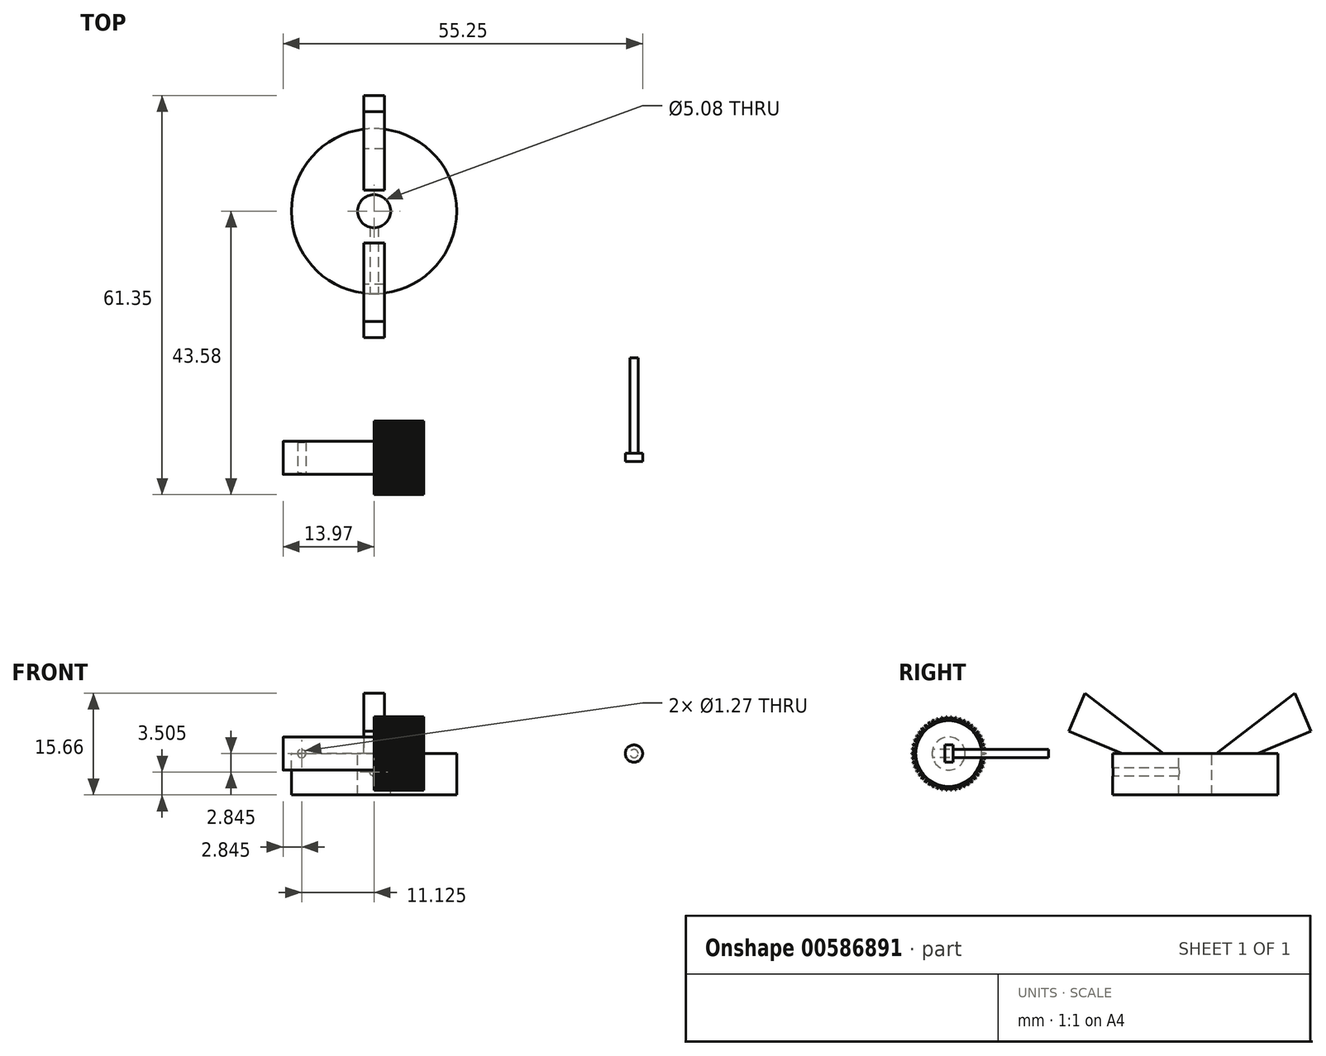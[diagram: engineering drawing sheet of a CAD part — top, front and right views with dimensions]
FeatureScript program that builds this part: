
annotation { "Feature Type Name" : "Feature", "Feature Type Description" : "" }
export const myFeature = defineFeature(function(context is Context, id is Id, definition is map)
    precondition{}
    {
        {
            var Q0;
            Q0=qCreatedBy(makeId("Right.planeOp"),FACE);
            var sketch = newSketch(context, id + "F0", { "sketchPlane" : qUnion([Q0])});
            skCircle(sketch, "E0", {"center": v(0, 0) * mm, "radius": 2.54 * mm});
            skCircle(sketch, "E1", {"center": v(0, 0) * mm, "radius": 5.08 * mm});
            skSolve(sketch);
        }
        {
            var Q0;
            Q0=makeQuery(id+"F0.imprint","IMPRINT",FACE,{"disambiguationData":[TD([[makeQuery(id+"F0.imprint","IMPRINT",EDGE,{"derivedFrom":sQuery(id+"F0.wireOp",EDGE,"E0")}),1.0]])]});
            extrude(context, id + "F1", {"entities" : qUnion([Q0]), "oppositeDirection" : true, "depth" : 13.97 * mm, "offsetDistance" : 25.4 * mm});
        }
        {
            var Q0;
            Q0=makeQuery(id+"F0.imprint","IMPRINT",FACE,{"disambiguationData":[TD([[makeQuery(id+"F0.imprint","IMPRINT",EDGE,{"derivedFrom":sQuery(id+"F0.wireOp",EDGE,"E0")}),-1.0]])]});
            var Q1;
            Q1=makeQuery(id+"F0.imprint","IMPRINT",FACE,{"disambiguationData":[TD([[makeQuery(id+"F0.imprint","IMPRINT",EDGE,{"derivedFrom":sQuery(id+"F0.wireOp",EDGE,"E0")}),1.0]])]});
            extrude(context, id + "F2", {"entities" : qUnion([Q0, Q1]), "operationType" : NewBodyOperationType.ADD, "depth" : 7.62 * mm, "offsetDistance" : 25.4 * mm});
        }
        {
            var Q0;
            Q0=qCreatedBy(makeId("Front.planeOp"),FACE);
            var sketch = newSketch(context, id + "F3", { "sketchPlane" : qUnion([Q0])});
            skPoint(sketch, "E2", {"position": v(-11.13, 0) * mm});
            skSolve(sketch);
        }
        {
            var Q0;
            Q0=qCreatedBy(makeId("Right.planeOp"),FACE);
            var sketch = newSketch(context, id + "F4", { "sketchPlane" : qUnion([Q0])});
            skLineSegment(sketch, "E3.bottom", {"start": v(5.03, -0.13) * mm, "end": v(5.54, -0.13) * mm});
            skLineSegment(sketch, "E3.top", {"start": v(5.03, 0.13) * mm, "end": v(5.54, 0.13) * mm});
            skLineSegment(sketch, "E3.left", {"start": v(5.03, -0.13) * mm, "end": v(5.03, 0.13) * mm});
            skPoint(sketch, "E3.middle", {"position": v(5.28, 0) * mm});
            skLineSegment(sketch, "E4", {"start": v(5.66, 0.06) * mm, "end": v(5.66, -0.06) * mm});
            skLineSegment(sketch, "E5", {"start": v(5.54, 0.13) * mm, "end": v(5.66, 0.06) * mm});
            skLineSegment(sketch, "E6", {"start": v(5.66, -0.06) * mm, "end": v(5.54, -0.13) * mm});
            skSolve(sketch);
        }
        {
            var Q0;
            Q0=makeQuery(id+"F4.imprint","IMPRINT",FACE,{"disambiguationData":[TD([[makeQuery(id+"F4.imprint","IMPRINT",EDGE,{"derivedFrom":sQuery(id+"F4.wireOp",EDGE,"E3.bottom")}),1.0]])]});
            extrude(context, id + "F5", {"entities" : qUnion([Q0]), "operationType" : NewBodyOperationType.ADD, "depth" : 7.62 * mm, "offsetDistance" : 25.4 * mm});
        }
        {
            var Q0;
            Q0=makeQuery(id+"F1.opExtrude","SWEPT_BODY",BODY,{"disambiguationData":[OSD([sQuery(id+"F0.wireOp",EDGE,"E0")])]});
            var Q1;
            Q1=sQuery(id+"F0.wireOp",EDGE,"E0");
            circularPattern(context, id + "F6", {"entities" : qUnion([Q0]), "axis" : qUnion([Q1]), "angle" : 360 * degree, "instanceCount" : 50, "equalSpace" : true});
        }
        {
            var Q0;
            Q0=sQuery(id+"F3.wireOp",VERTEX,"E2");
            var Q1;
            Q1=makeQuery(id+"F6.opPattern","COPY",BODY,{"derivedFrom":makeQuery(id+"F1.opExtrude","SWEPT_BODY",BODY,{"disambiguationData":[OSD([sQuery(id+"F0.wireOp",EDGE,"E0")])]}),"instanceName":"2"});
            hole(context, id + "F7", {"style" : HoleStyle.SIMPLE, "endStyle" : HoleEndStyle.BLIND, "holeDiameter" : 1.27 * mm, "majorDiameter" : 6.35 * mm, "holeDepth" : 508 * mm, "isTappedThrough" : true, "tappedDepth" : 12.7 * mm, "tapClearance" : 3, "startFromSketch" : true, "locations" : qUnion([Q0]), "scope" : qUnion([Q1])});
        }
        {
            var Q0;
            Q0=sQuery(id+"F3.wireOp",VERTEX,"E2");
            var Q1;
            Q1=makeQuery(id+"F6.opPattern","COPY",BODY,{"derivedFrom":makeQuery(id+"F1.opExtrude","SWEPT_BODY",BODY,{"disambiguationData":[OSD([sQuery(id+"F0.wireOp",EDGE,"E0")])]}),"instanceName":"2"});
            hole(context, id + "F8", {"style" : HoleStyle.SIMPLE, "endStyle" : HoleEndStyle.BLIND, "oppositeDirection" : true, "holeDiameter" : 1.27 * mm, "majorDiameter" : 6.35 * mm, "holeDepth" : 508 * mm, "isTappedThrough" : true, "tappedDepth" : 12.7 * mm, "tapClearance" : 3, "startFromSketch" : true, "locations" : qUnion([Q0]), "scope" : qUnion([Q1])});
        }
        {
            var Q0;
            Q0=qCreatedBy(makeId("Right.planeOp"),FACE);
            var sketch = newSketch(context, id + "F9", { "sketchPlane" : qUnion([Q0])});
            skLineSegment(sketch, "E7", {"start": v(20.96, 9.31) * mm, "end": v(18.49, 3.46) * mm});
            skLineSegment(sketch, "E8", {"start": v(47.5, 0) * mm, "end": v(55.7, 3.46) * mm});
            skLineSegment(sketch, "E9", {"start": v(55.7, 3.46) * mm, "end": v(53.22, 9.31) * mm});
            skLineSegment(sketch, "E10", {"start": v(53.22, 9.31) * mm, "end": v(41.16, 0) * mm});
            skLineSegment(sketch, "E11", {"start": v(20.96, 9.31) * mm, "end": v(33.02, 0) * mm});
            skLineSegment(sketch, "E12", {"start": v(33.02, 0) * mm, "end": v(26.67, 0) * mm});
            skLineSegment(sketch, "E13", {"start": v(26.67, 0) * mm, "end": v(18.49, 3.46) * mm});
            skLineSegment(sketch, "E14", {"start": v(41.16, 0) * mm, "end": v(47.5, 0) * mm});
            skLineSegment(sketch, "E15", {"start": v(24.39, 46.4) * mm, "end": v(24.39, 46.4) * mm});
            skSolve(sketch);
        }
        {
            var Q0;
            Q0=qCreatedBy(makeId("Top.planeOp"),FACE);
            var sketch = newSketch(context, id + "F10", { "sketchPlane" : qUnion([Q0])});
            skCircle(sketch, "E16", {"center": v(0, 37.92) * mm, "radius": 12.7 * mm});
            skSolve(sketch);
        }
        {
            var Q0;
            Q0=makeQuery(id+"F10.imprint","IMPRINT",FACE,{"disambiguationData":[TD([[makeQuery(id+"F10.imprint","IMPRINT",EDGE,{"derivedFrom":sQuery(id+"F10.wireOp",EDGE,"E16")}),1.0]])]});
            extrude(context, id + "F11", {"entities" : qUnion([Q0]), "oppositeDirection" : true, "depth" : 6.35 * mm, "offsetDistance" : 25.4 * mm});
        }
        {
            var Q0;
            Q0=makeQuery(id+"F9.imprint","IMPRINT",FACE,{"disambiguationData":[TD([[makeQuery(id+"F9.imprint","IMPRINT",EDGE,{"derivedFrom":sQuery(id+"F9.wireOp",EDGE,"E8")}),1.0]])]});
            var Q1;
            Q1=makeQuery(id+"F9.imprint","IMPRINT",FACE,{"disambiguationData":[TD([[makeQuery(id+"F9.imprint","IMPRINT",EDGE,{"derivedFrom":sQuery(id+"F9.wireOp",EDGE,"E7")}),1.0]])]});
            extrude(context, id + "F12", {"entities" : qUnion([Q0, Q1]), "operationType" : NewBodyOperationType.ADD, "endBound" : BoundingType.SYMMETRIC, "depth" : 3.17 * mm, "offsetDistance" : 25.4 * mm});
        }
        {
            var Q0;
            Q0=sQuery(id+"F10.wireOp",VERTEX,"E16.center");
            var Q1;
            Q1=makeQuery(id+"F11.opExtrude","SWEPT_BODY",BODY,{"disambiguationData":[OSD([sQuery(id+"F10.wireOp",EDGE,"E16")])]});
            hole(context, id + "F13", {"style" : HoleStyle.SIMPLE, "endStyle" : HoleEndStyle.BLIND, "holeDiameter" : 5.08 * mm, "majorDiameter" : 6.35 * mm, "holeDepth" : 508 * mm, "isTappedThrough" : true, "tappedDepth" : 12.7 * mm, "tapClearance" : 3, "startFromSketch" : true, "locations" : qUnion([Q0]), "scope" : qUnion([Q1])});
        }
        {
            var Q0;
            Q0=qCreatedBy(makeId("Front.planeOp"),FACE);
            var sketch = newSketch(context, id + "F14", { "sketchPlane" : qUnion([Q0])});
            skPoint(sketch, "E17", {"position": v(0, -2.84) * mm});
            skSolve(sketch);
        }
        {
            var Q0;
            Q0=sQuery(id+"F14.wireOp",VERTEX,"E17");
            var Q1;
            Q1=makeQuery(id+"F11.opExtrude","SWEPT_BODY",BODY,{"disambiguationData":[OSD([sQuery(id+"F10.wireOp",EDGE,"E16")])]});
            hole(context, id + "F15", {"style" : HoleStyle.SIMPLE, "endStyle" : HoleEndStyle.BLIND, "holeDiameter" : 1.27 * mm, "majorDiameter" : 6.35 * mm, "holeDepth" : 38.1 * mm, "isTappedThrough" : true, "tappedDepth" : 12.7 * mm, "tapClearance" : 3, "startFromSketch" : true, "locations" : qUnion([Q0]), "scope" : qUnion([Q1])});
        }
        {
            var Q0;
            Q0=qCreatedBy(makeId("Top.planeOp"),FACE);
            var sketch = newSketch(context, id + "F16", { "sketchPlane" : qUnion([Q0])});
            skLineSegment(sketch, "E18.bottom", {"start": v(40.58, 0.7) * mm, "end": v(39.95, 0.7) * mm});
            skLineSegment(sketch, "E18.top", {"start": v(40.58, 15.35) * mm, "end": v(39.95, 15.35) * mm});
            skLineSegment(sketch, "E18.left", {"start": v(40.58, 0.7) * mm, "end": v(40.58, 15.35) * mm});
            skLineSegment(sketch, "E18.right", {"start": v(39.95, 0.7) * mm, "end": v(39.95, 15.35) * mm});
            skPoint(sketch, "E18.middle", {"position": v(40.26, 8.02) * mm});
            skLineSegment(sketch, "E19.bottom", {"start": v(39.95, 0.7) * mm, "end": v(41.28, 0.7) * mm});
            skLineSegment(sketch, "E19.top", {"start": v(39.95, -0.58) * mm, "end": v(41.28, -0.58) * mm});
            skLineSegment(sketch, "E19.left", {"start": v(39.95, 0.7) * mm, "end": v(39.95, -0.58) * mm});
            skLineSegment(sketch, "E19.right", {"start": v(41.28, 0.7) * mm, "end": v(41.28, -0.58) * mm});
            skSolve(sketch);
        }
        {
            var Q0;
            Q0=makeQuery(id+"F16.imprint","IMPRINT",FACE,{"disambiguationData":[TD([[makeQuery(id+"F16.imprint","IMPRINT",EDGE,{"derivedFrom":sQuery(id+"F16.wireOp",EDGE,"E19.top")}),1.0]])]});
            var Q1;
            Q1=makeQuery(id+"F16.imprint","IMPRINT",FACE,{"disambiguationData":[TD([[makeQuery(id+"F16.imprint","IMPRINT",EDGE,{"derivedFrom":sQuery(id+"F16.wireOp",EDGE,"E18.top")}),1.0]])]});
            var Q2;
            Q2=sQuery(id+"F16.wireOp",EDGE,"E18.right");
            revolve(context, id + "F17", {"entities" : qUnion([Q0, Q1]), "axis" : qUnion([Q2]), "revolveType" : RevolveType.FULL});
        }
    });
